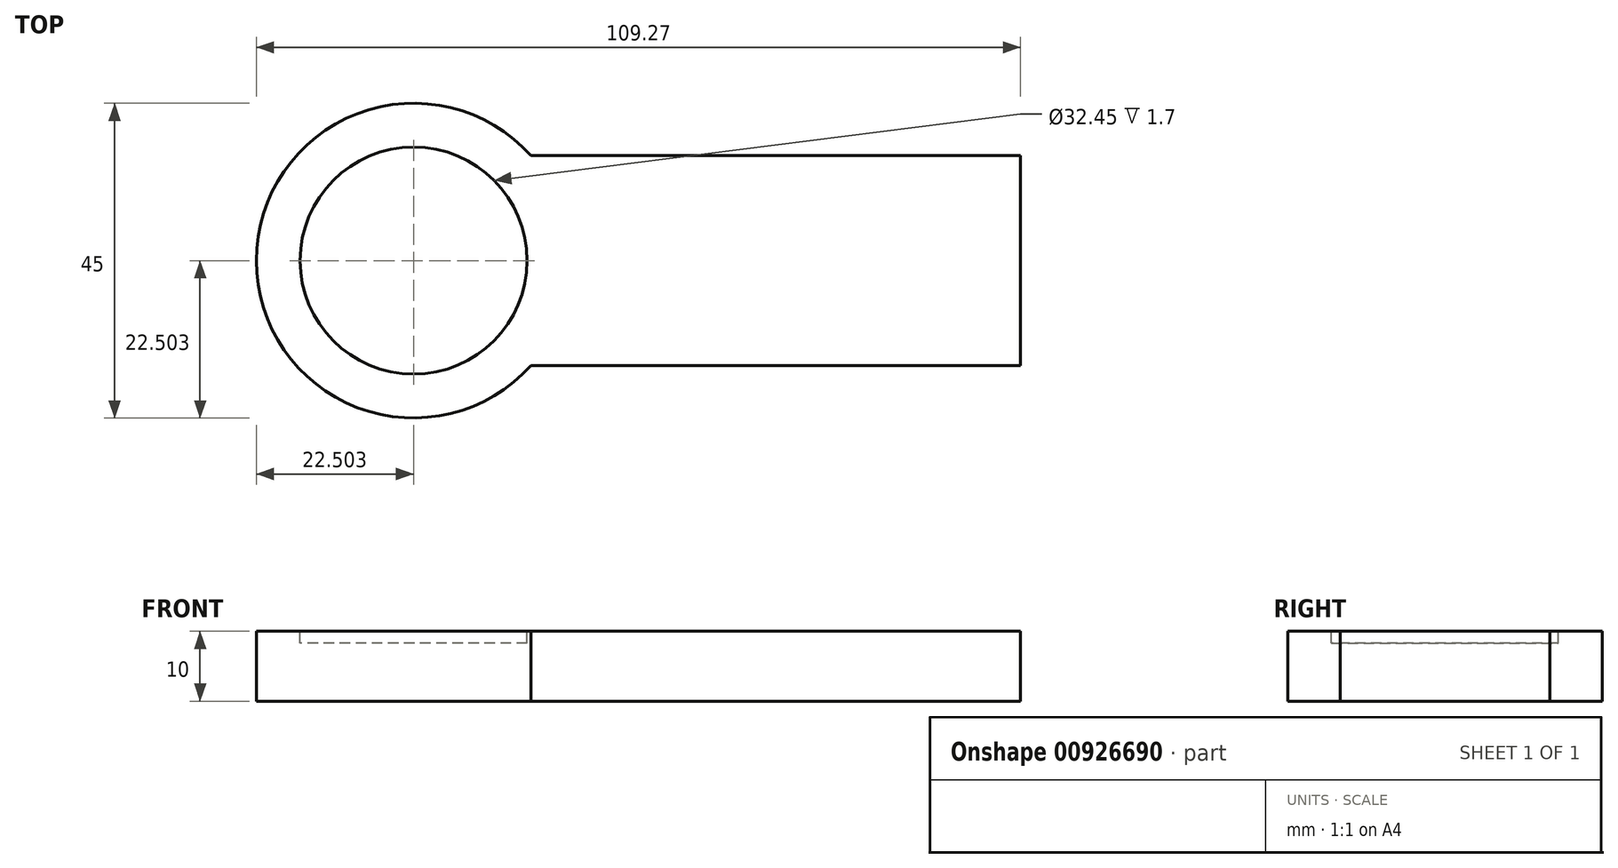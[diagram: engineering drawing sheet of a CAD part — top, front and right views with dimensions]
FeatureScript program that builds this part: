
annotation { "Feature Type Name" : "Feature", "Feature Type Description" : "" }
export const myFeature = defineFeature(function(context is Context, id is Id, definition is map)
    precondition{}
    {
        {
            var Q0;
            Q0=qCreatedBy(makeId("Top.planeOp"),FACE);
            var sketch = newSketch(context, id + "F0", { "sketchPlane" : qUnion([Q0])});
            skLineSegment(sketch, "E0.bottom", {"start": v(-95.12, 25.44) * mm, "end": v(-25.12, 25.44) * mm});
            skLineSegment(sketch, "E0.top", {"start": v(-95.12, -4.56) * mm, "end": v(-25.12, -4.56) * mm});
            skLineSegment(sketch, "E0.left", {"start": v(-95.12, 25.44) * mm, "end": v(-95.12, -4.56) * mm});
            skLineSegment(sketch, "E0.right", {"start": v(-25.12, 25.44) * mm, "end": v(-25.12, -4.56) * mm});
            skArc(sketch, "E1", {"start": v(-95.12, 25.44) * mm, "mid": v(-134.39, 10.44) * mm, "end": v(-95.12, -4.56) * mm});
            skPoint(sketch, "E1.third.point", {"position": v(-133.24, 3.34) * mm});
            skArc(sketch, "E2", {"start": v(-95.12, 14.95) * mm, "mid": v(-129.25, 10.44) * mm, "end": v(-95.12, 5.94) * mm});
            skSolve(sketch);
        }
        {
            var Q0;
            {var subQ5=sQuery(id+"F0.wireOp",EDGE,"E0.bottom");Q0=makeQuery(id+"F0.imprint","IMPRINT",FACE,{"disambiguationData":[TD([[makeQuery(id+"F0.imprint","IMPRINT",EDGE,{"derivedFrom":subQ5}),-1.0]])]});}
            var Q1;
            {var subQ0=sQuery(id+"F0.wireOp",EDGE,"E2");Q1=makeQuery(id+"F0.imprint","IMPRINT",FACE,{"disambiguationData":[TD([[makeQuery(id+"F0.imprint","IMPRINT",EDGE,{"derivedFrom":subQ0}),1.0]])]});}
            var Q2;
            {var subQ0=sQuery(id+"F0.wireOp",EDGE,"E1");Q2=makeQuery(id+"F0.imprint","IMPRINT",FACE,{"disambiguationData":[TD([[makeQuery(id+"F0.imprint","IMPRINT",EDGE,{"derivedFrom":subQ0}),1.0]])]});}
            extrude(context, id + "F1", {"entities" : qUnion([Q0, Q1, Q2]), "depth" : 10 * mm, "offsetDistance" : 25 * mm});
        }
        {
            var Q0;
            Q0=makeQuery(id+"F1.opExtrude","CAP_FACE",FACE,{"disambiguationData":[OSD([sQuery(id+"F0.wireOp",EDGE,"E0.bottom"),sQuery(id+"F0.wireOp",EDGE,"E0.top"),sQuery(id+"F0.wireOp",EDGE,"E0.right"),sQuery(id+"F0.wireOp",EDGE,"E1")])],"isStart":false});
            var sketch = newSketch(context, id + "F2", { "sketchPlane" : qUnion([Q0])});
            skCircle(sketch, "E3", {"center": v(-111.89, 10.44) * mm, "radius": 16.23 * mm});
            skSolve(sketch);
        }
        {
            var Q0;
            Q0 = qSketchRegion(id + "F2", true);
            extrude(context, id + "F3", {"entities" : qUnion([Q0]), "operationType" : NewBodyOperationType.REMOVE, "oppositeDirection" : true, "depth" : 1.7 * mm, "offsetDistance" : 25 * mm});
        }
    });
